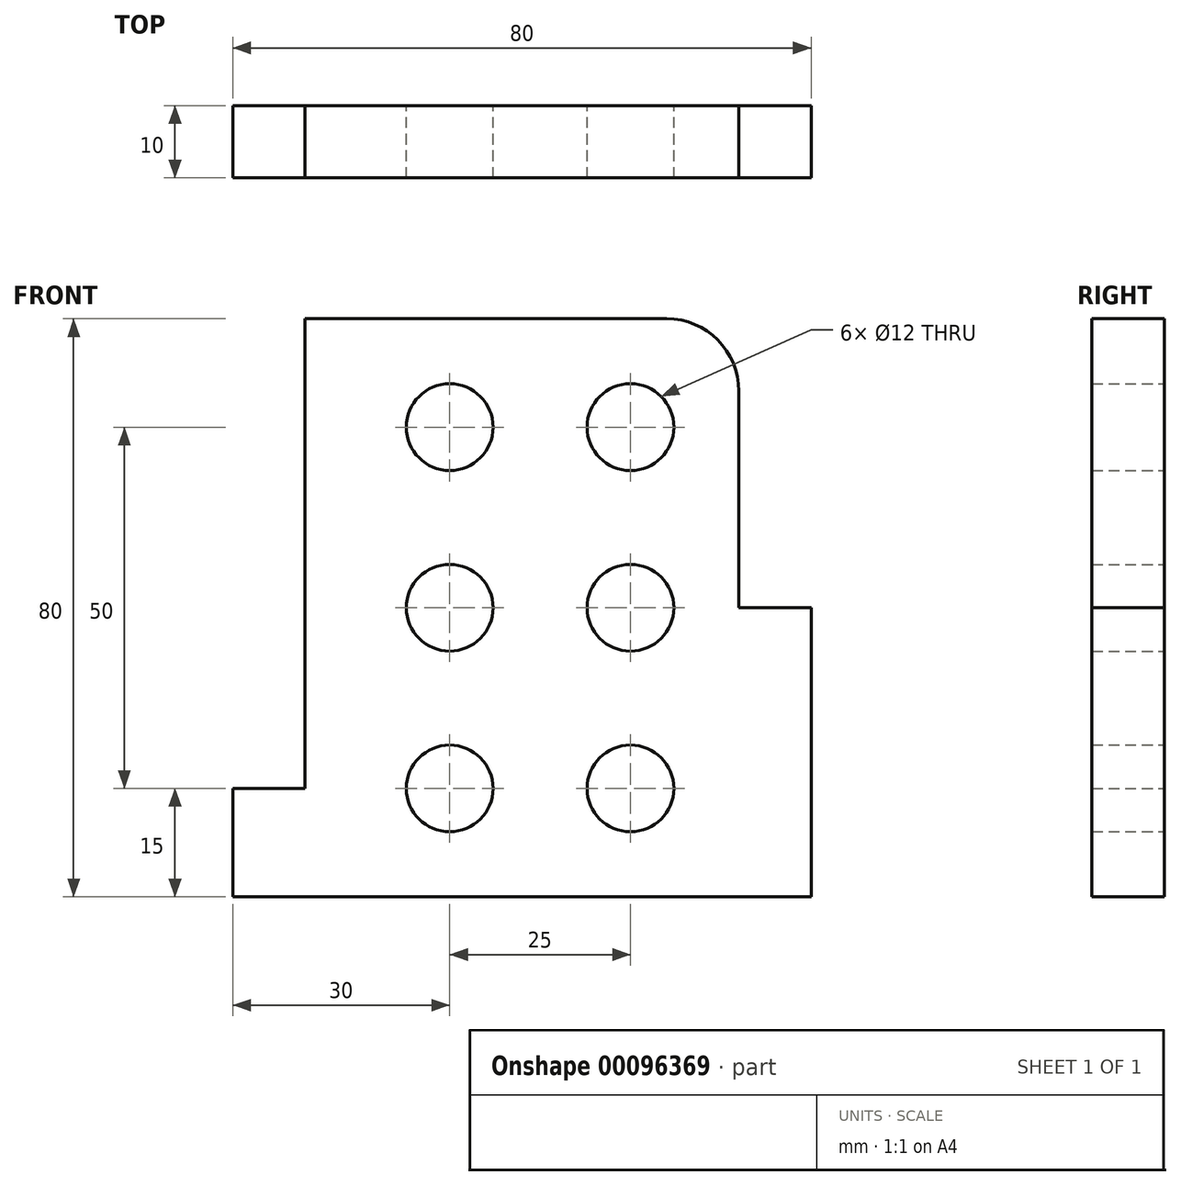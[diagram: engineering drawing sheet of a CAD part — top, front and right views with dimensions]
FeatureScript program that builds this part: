
annotation { "Feature Type Name" : "Feature", "Feature Type Description" : "" }
export const myFeature = defineFeature(function(context is Context, id is Id, definition is map)
    precondition{}
    {
        {
            var Q0;
            Q0=qCreatedBy(makeId("Front.planeOp"),FACE);
            var sketch = newSketch(context, id + "F0", { "sketchPlane" : qUnion([Q0])});
            skLineSegment(sketch, "E0", {"start": v(0, 0) * mm, "end": v(0, 15) * mm});
            skLineSegment(sketch, "E1", {"start": v(0, 15) * mm, "end": v(10, 15) * mm});
            skLineSegment(sketch, "E2", {"start": v(10, 15) * mm, "end": v(10, 80) * mm});
            skLineSegment(sketch, "E3", {"start": v(10, 80) * mm, "end": v(60, 80) * mm});
            skLineSegment(sketch, "E4", {"start": v(70, 70) * mm, "end": v(70, 40) * mm});
            skLineSegment(sketch, "E5", {"start": v(70, 40) * mm, "end": v(80, 40) * mm});
            skLineSegment(sketch, "E6", {"start": v(80, 40) * mm, "end": v(80, 0) * mm});
            skLineSegment(sketch, "E7", {"start": v(80, 0) * mm, "end": v(0, 0) * mm});
            skPoint(sketch, "E8.visualSharp", {"position": v(70, 80) * mm});
            skArc(sketch, "E8.filletArc", {"start": v(70, 70) * mm, "mid": v(67.07, 77.07) * mm, "end": v(60, 80) * mm});
            skCircle(sketch, "E9", {"center": v(30, 15) * mm, "radius": 6 * mm});
            skCircle(sketch, "E10", {"center": v(55, 15) * mm, "radius": 6 * mm});
            skCircle(sketch, "E11", {"center": v(55, 40) * mm, "radius": 6 * mm});
            skCircle(sketch, "E12", {"center": v(55, 65) * mm, "radius": 6 * mm});
            skCircle(sketch, "E13", {"center": v(30, 65) * mm, "radius": 6 * mm});
            skCircle(sketch, "E14", {"center": v(30, 40) * mm, "radius": 6 * mm});
            skSolve(sketch);
        }
        {
            var Q0;
            Q0=makeQuery(id+"F0.imprint","IMPRINT",FACE,{"disambiguationData":[TD([[makeQuery(id+"F0.imprint","IMPRINT",EDGE,{"derivedFrom":sQuery(id+"F0.wireOp",EDGE,"E0")}),-1.0]])]});
            extrude(context, id + "F1", {"entities" : qUnion([Q0]), "depth" : 10 * mm});
        }
    });
